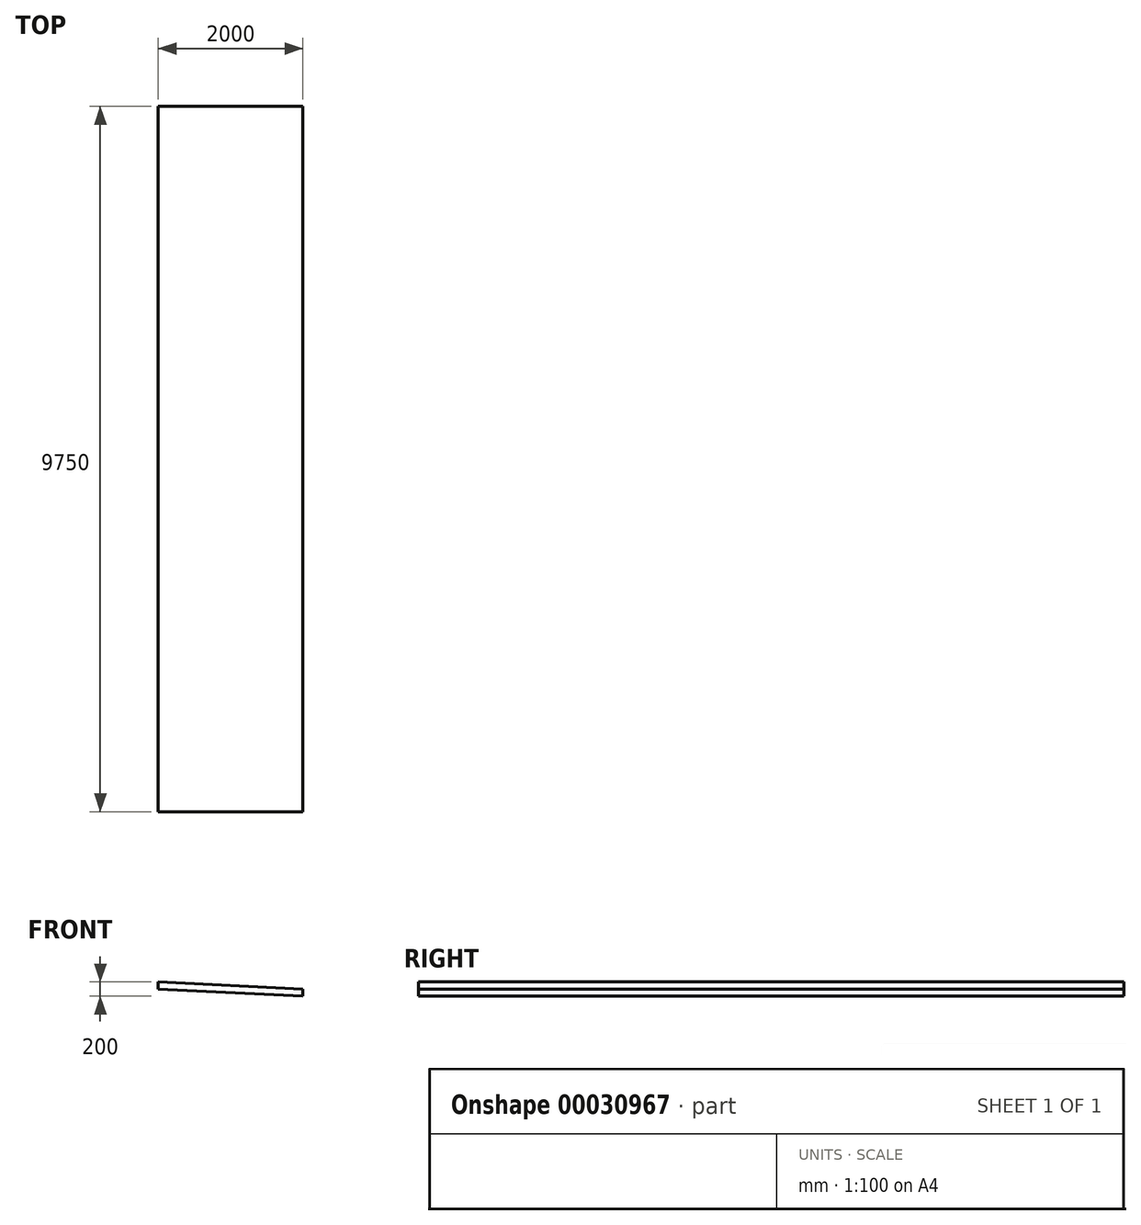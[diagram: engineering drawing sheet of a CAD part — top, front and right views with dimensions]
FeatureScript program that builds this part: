
annotation { "Feature Type Name" : "Feature", "Feature Type Description" : "" }
export const myFeature = defineFeature(function(context is Context, id is Id, definition is map)
    precondition{}
    {
        {
            var Q0;
            Q0=qCreatedBy(makeId("Front.planeOp"),FACE);
            var sketch = newSketch(context, id + "F0", { "sketchPlane" : qUnion([Q0])});
            skLineSegment(sketch, "E0", {"start": v(0, 0) * mm, "end": v(0, 100) * mm});
            skLineSegment(sketch, "E1", {"start": v(0, 100) * mm, "end": v(2000, 0) * mm});
            skLineSegment(sketch, "E2", {"start": v(2000, 0) * mm, "end": v(2000, -100) * mm});
            skLineSegment(sketch, "E3", {"start": v(2000, -100) * mm, "end": v(0, 0) * mm});
            skSolve(sketch);
        }
        {
            var Q0;
            Q0=makeQuery(id+"F0.imprint","IMPRINT",FACE,{"disambiguationData":[TD([[makeQuery(id+"F0.imprint","IMPRINT",EDGE,{"derivedFrom":sQuery(id+"F0.wireOp",EDGE,"E0")}),-1.0]])]});
            extrude(context, id + "F1", {"entities" : qUnion([Q0]), "depth" : 9750 * mm});
        }
    });
